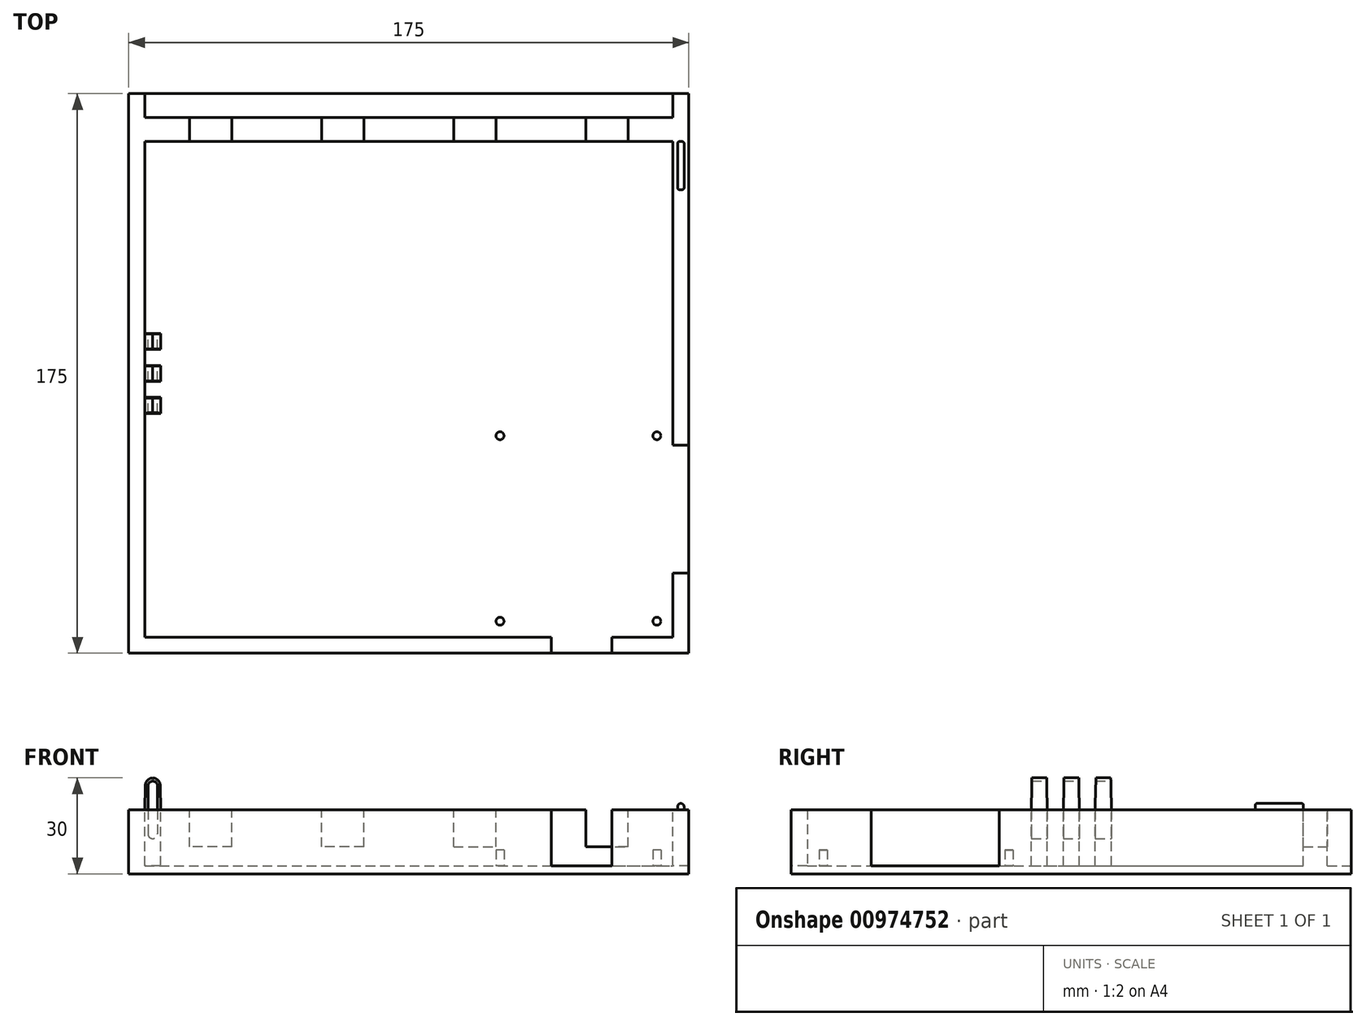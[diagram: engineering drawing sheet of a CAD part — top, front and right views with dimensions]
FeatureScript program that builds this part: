
annotation { "Feature Type Name" : "Feature", "Feature Type Description" : "" }
export const myFeature = defineFeature(function(context is Context, id is Id, definition is map)
    precondition{}
    {
        {
            var Q0;
            Q0=qCreatedBy(makeId("Top.planeOp"),FACE);
            var sketch = newSketch(context, id + "F0", { "sketchPlane" : qUnion([Q0])});
            skLineSegment(sketch, "E0.bottom", {"start": v(87.5, 87.5) * mm, "end": v(-87.5, 87.5) * mm});
            skLineSegment(sketch, "E0.top", {"start": v(87.5, -87.5) * mm, "end": v(-87.5, -87.5) * mm});
            skLineSegment(sketch, "E0.left", {"start": v(87.5, 87.5) * mm, "end": v(87.5, -87.5) * mm});
            skLineSegment(sketch, "E0.right", {"start": v(-87.5, 87.5) * mm, "end": v(-87.5, -87.5) * mm});
            skPoint(sketch, "E0.middle", {"position": v(0, 0) * mm});
            skSolve(sketch);
        }
        {
            var Q0;
            Q0 = qSketchRegion(id + "F0", true);
            extrude(context, id + "F1", {"entities" : qUnion([Q0]), "depth" : 20 * mm, "offsetDistance" : 25 * mm});
        }
        {
            var Q0;
            Q0=makeQuery(id+"F1.opExtrude","CAP_FACE",FACE,{"disambiguationData":[OSD([sQuery(id+"F0.wireOp",EDGE,"E0.bottom"),sQuery(id+"F0.wireOp",EDGE,"E0.top"),sQuery(id+"F0.wireOp",EDGE,"E0.left"),sQuery(id+"F0.wireOp",EDGE,"E0.right")])],"isStart":false});
            var sketch = newSketch(context, id + "F2", { "sketchPlane" : qUnion([Q0])});
            skLineSegment(sketch, "E1.bottom", {"start": v(-82.5, -82.5) * mm, "end": v(82.5, -82.5) * mm});
            skLineSegment(sketch, "E1.top", {"start": v(-82.5, 72.5) * mm, "end": v(82.5, 72.5) * mm});
            skLineSegment(sketch, "E1.left", {"start": v(-82.5, -82.5) * mm, "end": v(-82.5, 72.5) * mm});
            skLineSegment(sketch, "E1.right", {"start": v(82.5, -82.5) * mm, "end": v(82.5, 72.5) * mm});
            skSolve(sketch);
        }
        {
            var Q0;
            Q0 = qSketchRegion(id + "F2", true);
            extrude(context, id + "F3", {"entities" : qUnion([Q0]), "operationType" : NewBodyOperationType.REMOVE, "oppositeDirection" : true, "depth" : 17.5 * mm, "offsetDistance" : 25 * mm});
        }
        {
            var Q0;
            Q0=makeQuery(id+"F3.boolean.opBoolean","COPY",FACE,{"derivedFrom":makeQuery(id+"F3.opExtrude","CAP_FACE",FACE,{"disambiguationData":[OSD([sQuery(id+"F2.wireOp",EDGE,"E1.bottom"),sQuery(id+"F2.wireOp",EDGE,"E1.top"),sQuery(id+"F2.wireOp",EDGE,"E1.left"),sQuery(id+"F2.wireOp",EDGE,"E1.right")])],"isStart":false})});
            var sketch = newSketch(context, id + "F4", { "sketchPlane" : qUnion([Q0])});
            skCircle(sketch, "E2", {"center": v(28.5, -77.5) * mm, "radius": 1.25 * mm});
            skLineSegment(sketch, "E3", {"start": v(28.5, -77.5) * mm, "end": v(77.5, -77.5) * mm, "construction": true});
            skLineSegment(sketch, "E4", {"start": v(28.5, -77.5) * mm, "end": v(28.5, -6.05) * mm, "construction": true});
            skCircle(sketch, "E5", {"center": v(28.5, -19.5) * mm, "radius": 1.25 * mm});
            skCircle(sketch, "E6", {"center": v(77.5, -77.5) * mm, "radius": 1.25 * mm});
            skLineSegment(sketch, "E7", {"start": v(23.98, -19.5) * mm, "end": v(28.5, -19.5) * mm, "construction": true});
            skLineSegment(sketch, "E8", {"start": v(77.5, -77.5) * mm, "end": v(77.5, -2.25) * mm, "construction": true});
            skCircle(sketch, "E9", {"center": v(77.5, -19.5) * mm, "radius": 1.25 * mm});
            skSolve(sketch);
        }
        {
            var Q0;
            Q0 = qSketchRegion(id + "F4", true);
            extrude(context, id + "F5", {"entities" : qUnion([Q0]), "operationType" : NewBodyOperationType.ADD, "depth" : 5 * mm, "offsetDistance" : 25 * mm});
        }
        {
            var Q0;
            Q0=makeQuery(id+"F1.opExtrude","CAP_FACE",FACE,{"disambiguationData":[OSD([sQuery(id+"F0.wireOp",EDGE,"E0.bottom"),sQuery(id+"F0.wireOp",EDGE,"E0.top"),sQuery(id+"F0.wireOp",EDGE,"E0.left"),sQuery(id+"F0.wireOp",EDGE,"E0.right")])],"isStart":false});
            var sketch = newSketch(context, id + "F6", { "sketchPlane" : qUnion([Q0])});
            skLineSegment(sketch, "E10.bottom", {"start": v(-82.5, 80) * mm, "end": v(82.5, 80) * mm});
            skLineSegment(sketch, "E10.top", {"start": v(-82.5, 87.5) * mm, "end": v(82.5, 87.5) * mm});
            skLineSegment(sketch, "E10.left", {"start": v(-82.5, 80) * mm, "end": v(-82.5, 87.5) * mm});
            skLineSegment(sketch, "E10.right", {"start": v(82.5, 80) * mm, "end": v(82.5, 87.5) * mm});
            skSolve(sketch);
        }
        {
            var Q0;
            Q0 = qSketchRegion(id + "F6", true);
            extrude(context, id + "F7", {"entities" : qUnion([Q0]), "operationType" : NewBodyOperationType.REMOVE, "oppositeDirection" : true, "depth" : 17.5 * mm, "offsetDistance" : 25 * mm});
        }
        {
            var Q0;
            Q0=makeQuery(id+"F7.boolean.opBoolean","COPY",FACE,{"derivedFrom":makeQuery(id+"F7.opExtrude","SWEPT_FACE",FACE,{"disambiguationData":[OSD([sQuery(id+"F6.wireOp",EDGE,"E10.bottom")])]})});
            var sketch = newSketch(context, id + "F8", { "sketchPlane" : qUnion([Q0])});
            skLineSegment(sketch, "E11", {"start": v(-82.5, 11.25) * mm, "end": v(82.5, 11.25) * mm, "construction": true});
            skLineSegment(sketch, "E12", {"start": v(0, 20) * mm, "end": v(0, 2.5) * mm, "construction": true});
            skPoint(sketch, "E13", {"position": v(0, 11.25) * mm});
            skPoint(sketch, "E14", {"position": v(41.25, 11.25) * mm});
            skPoint(sketch, "E15", {"position": v(-41.25, 11.25) * mm});
            skPoint(sketch, "E16", {"position": v(-61.87, 11.25) * mm});
            skPoint(sketch, "E17", {"position": v(-20.62, 11.25) * mm});
            skPoint(sketch, "E18", {"position": v(20.62, 11.25) * mm});
            skPoint(sketch, "E19", {"position": v(61.87, 11.25) * mm});
            skLineSegment(sketch, "E20.bottom", {"start": v(-55.27, 14.1) * mm, "end": v(-68.47, 14.1) * mm});
            skLineSegment(sketch, "E20.top", {"start": v(-55.27, 8.4) * mm, "end": v(-68.47, 8.4) * mm});
            skLineSegment(sketch, "E20.left", {"start": v(-55.27, 14.1) * mm, "end": v(-55.27, 8.4) * mm});
            skLineSegment(sketch, "E20.right", {"start": v(-68.47, 14.1) * mm, "end": v(-68.47, 8.4) * mm});
            skLineSegment(sketch, "E21.bottom", {"start": v(-27.22, 14.1) * mm, "end": v(-14.02, 14.1) * mm});
            skLineSegment(sketch, "E21.top", {"start": v(-27.22, 8.4) * mm, "end": v(-14.02, 8.4) * mm});
            skLineSegment(sketch, "E21.left", {"start": v(-27.22, 14.1) * mm, "end": v(-27.22, 8.4) * mm});
            skLineSegment(sketch, "E21.right", {"start": v(-14.02, 14.1) * mm, "end": v(-14.02, 8.4) * mm});
            skLineSegment(sketch, "E22.bottom", {"start": v(27.22, 14.1) * mm, "end": v(14.02, 14.1) * mm});
            skLineSegment(sketch, "E22.top", {"start": v(27.22, 8.4) * mm, "end": v(14.02, 8.4) * mm});
            skLineSegment(sketch, "E22.left", {"start": v(27.22, 14.1) * mm, "end": v(27.22, 8.4) * mm});
            skLineSegment(sketch, "E22.right", {"start": v(14.02, 14.1) * mm, "end": v(14.02, 8.4) * mm});
            skLineSegment(sketch, "E23.bottom", {"start": v(68.47, 14.1) * mm, "end": v(55.27, 14.1) * mm});
            skLineSegment(sketch, "E23.top", {"start": v(68.47, 8.4) * mm, "end": v(55.27, 8.4) * mm});
            skLineSegment(sketch, "E23.left", {"start": v(68.47, 14.1) * mm, "end": v(68.47, 8.4) * mm});
            skLineSegment(sketch, "E23.right", {"start": v(55.27, 14.1) * mm, "end": v(55.27, 8.4) * mm});
            skSolve(sketch);
        }
        {
            var Q0;
            Q0 = qSketchRegion(id + "F8", true);
            extrude(context, id + "F9", {"entities" : qUnion([Q0]), "operationType" : NewBodyOperationType.REMOVE, "oppositeDirection" : true, "depth" : 8.5 * mm, "offsetDistance" : 25 * mm});
        }
        {
            var Q0;
            Q0=makeQuery(id+"F1.opExtrude","CAP_FACE",FACE,{"disambiguationData":[OSD([sQuery(id+"F0.wireOp",EDGE,"E0.bottom"),sQuery(id+"F0.wireOp",EDGE,"E0.top"),sQuery(id+"F0.wireOp",EDGE,"E0.left"),sQuery(id+"F0.wireOp",EDGE,"E0.right")])],"isStart":false});
            var sketch = newSketch(context, id + "F10", { "sketchPlane" : qUnion([Q0])});
            skLineSegment(sketch, "E24.bottom", {"start": v(-77.5, -2.5) * mm, "end": v(-82.5, -2.5) * mm});
            skLineSegment(sketch, "E24.top", {"start": v(-77.5, 2.5) * mm, "end": v(-82.5, 2.5) * mm});
            skLineSegment(sketch, "E24.left", {"start": v(-77.5, -2.5) * mm, "end": v(-77.5, 2.5) * mm});
            skLineSegment(sketch, "E24.right", {"start": v(-82.5, -2.5) * mm, "end": v(-82.5, 2.5) * mm});
            skLineSegment(sketch, "E25.bottom", {"start": v(-77.5, 7.5) * mm, "end": v(-82.5, 7.5) * mm});
            skLineSegment(sketch, "E25.top", {"start": v(-77.5, 12.5) * mm, "end": v(-82.5, 12.5) * mm});
            skLineSegment(sketch, "E25.left", {"start": v(-77.5, 7.5) * mm, "end": v(-77.5, 12.5) * mm});
            skLineSegment(sketch, "E25.right", {"start": v(-82.5, 7.5) * mm, "end": v(-82.5, 12.5) * mm});
            skLineSegment(sketch, "E26.bottom", {"start": v(-77.5, -12.5) * mm, "end": v(-82.5, -12.5) * mm});
            skLineSegment(sketch, "E26.top", {"start": v(-77.5, -7.5) * mm, "end": v(-82.5, -7.5) * mm});
            skLineSegment(sketch, "E26.left", {"start": v(-77.5, -12.5) * mm, "end": v(-77.5, -7.5) * mm});
            skLineSegment(sketch, "E26.right", {"start": v(-82.5, -12.5) * mm, "end": v(-82.5, -7.5) * mm});
            skSolve(sketch);
        }
        {
            var Q0;
            Q0 = qSketchRegion(id + "F10", true);
            extrude(context, id + "F11", {"entities" : qUnion([Q0]), "operationType" : NewBodyOperationType.ADD, "oppositeDirection" : true, "depth" : 17.5 * mm, "offsetDistance" : 25 * mm, "hasSecondDirection" : true, "secondDirectionOppositeDirection" : false, "secondDirectionDepth" : 10 * mm, "hasSecondDirectionDraft" : true, "secondDirectionDraftAngle" : 1 * degree, "secondDirectionDraftPullDirection" : true});
        }
        {
            var Q0;
            Q0=makeQuery(id+"F11.opExtrude","CAP_EDGE",EDGE,{"disambiguationData":[OSD([sQuery(id+"F10.wireOp",EDGE,"E25.right")])],"isStart":true});
            var Q1;
            Q1=makeQuery(id+"F11.opExtrude","CAP_EDGE",EDGE,{"disambiguationData":[OSD([sQuery(id+"F10.wireOp",EDGE,"E25.left")])],"isStart":true});
            var Q2;
            Q2=makeQuery(id+"F11.opExtrude","CAP_EDGE",EDGE,{"disambiguationData":[OSD([sQuery(id+"F10.wireOp",EDGE,"E24.left")])],"isStart":true});
            var Q3;
            Q3=makeQuery(id+"F11.opExtrude","CAP_EDGE",EDGE,{"disambiguationData":[OSD([sQuery(id+"F10.wireOp",EDGE,"E24.right")])],"isStart":true});
            var Q4;
            Q4=makeQuery(id+"F11.opExtrude","CAP_EDGE",EDGE,{"disambiguationData":[OSD([sQuery(id+"F10.wireOp",EDGE,"E26.right")])],"isStart":true});
            var Q5;
            Q5=makeQuery(id+"F11.opExtrude","CAP_EDGE",EDGE,{"disambiguationData":[OSD([sQuery(id+"F10.wireOp",EDGE,"E26.left")])],"isStart":true});
            fillet(context, id + "F12", {"entities" : qUnion([Q0, Q1, Q2, Q3, Q4, Q5]), "radius" : 2.5 * mm, "tangentPropagation" : true, "allowEdgeOverflow" : false});
        }
        {
            var Q0;
            Q0=makeQuery(id+"F11.*.split.splitOp","SPLIT",FACE,{"derivedFrom":makeQuery(id+"F11.opExtrude","SWEPT_FACE",FACE,{"disambiguationData":[OSD([sQuery(id+"F10.wireOp",EDGE,"E25.top")])]})});
            var sketch = newSketch(context, id + "F13", { "sketchPlane" : qUnion([Q0])});
            skLineSegment(sketch, "E27.left", {"start": v(81.5, 27.5) * mm, "end": v(81.5, 12.5) * mm});
            skLineSegment(sketch, "E27.right", {"start": v(78.5, 27.5) * mm, "end": v(78.5, 12.5) * mm});
            skPoint(sketch, "E27.middle", {"position": v(80, 20) * mm});
            skArc(sketch, "E28", {"start": v(81.5, 27.5) * mm, "mid": v(80, 29) * mm, "end": v(78.5, 27.5) * mm});
            skArc(sketch, "E29", {"start": v(78.5, 12.5) * mm, "mid": v(80, 11) * mm, "end": v(81.5, 12.5) * mm});
            skSolve(sketch);
        }
        {
            var Q0;
            Q0 = qSketchRegion(id + "F13", true);
            extrude(context, id + "F14", {"entities" : qUnion([Q0]), "operationType" : NewBodyOperationType.REMOVE, "oppositeDirection" : true, "depth" : 25 * mm, "offsetDistance" : 25 * mm});
        }
        {
            var Q0;
            Q0=makeQuery(id+"F1.opExtrude","CAP_FACE",FACE,{"disambiguationData":[OSD([sQuery(id+"F0.wireOp",EDGE,"E0.bottom"),sQuery(id+"F0.wireOp",EDGE,"E0.top"),sQuery(id+"F0.wireOp",EDGE,"E0.left"),sQuery(id+"F0.wireOp",EDGE,"E0.right")])],"isStart":false});
            var sketch = newSketch(context, id + "F15", { "sketchPlane" : qUnion([Q0])});
            skLineSegment(sketch, "E30.bottom", {"start": v(63.5, -73.66) * mm, "end": v(44.5, -73.66) * mm});
            skLineSegment(sketch, "E30.top", {"start": v(63.5, -91.34) * mm, "end": v(44.5, -91.34) * mm});
            skLineSegment(sketch, "E30.left", {"start": v(63.5, -73.66) * mm, "end": v(63.5, -91.34) * mm});
            skLineSegment(sketch, "E30.right", {"start": v(44.5, -73.66) * mm, "end": v(44.5, -91.34) * mm});
            skPoint(sketch, "E30.middle", {"position": v(54, -82.5) * mm});
            skLineSegment(sketch, "E31.bottom", {"start": v(98.64, -22.5) * mm, "end": v(66.36, -22.5) * mm});
            skLineSegment(sketch, "E31.top", {"start": v(98.64, -62.5) * mm, "end": v(66.36, -62.5) * mm});
            skLineSegment(sketch, "E31.left", {"start": v(98.64, -22.5) * mm, "end": v(98.64, -62.5) * mm});
            skLineSegment(sketch, "E31.right", {"start": v(66.36, -22.5) * mm, "end": v(66.36, -62.5) * mm});
            skPoint(sketch, "E31.middle", {"position": v(82.5, -42.5) * mm});
            skSolve(sketch);
        }
        {
            var Q0;
            Q0 = qSketchRegion(id + "F15", true);
            extrude(context, id + "F16", {"entities" : qUnion([Q0]), "operationType" : NewBodyOperationType.REMOVE, "oppositeDirection" : true, "depth" : 17.5 * mm, "offsetDistance" : 25 * mm});
        }
        {
            var Q0;
            Q0=makeQuery(id+"F7.boolean.opBoolean","COPY",FACE,{"derivedFrom":makeQuery(id+"F7.opExtrude","SWEPT_FACE",FACE,{"disambiguationData":[OSD([sQuery(id+"F6.wireOp",EDGE,"E10.bottom")])]})});
            var sketch = newSketch(context, id + "F17", { "sketchPlane" : qUnion([Q0])});
            skLineSegment(sketch, "E32", {"start": v(-68.47, 14.1) * mm, "end": v(-68.47, 20) * mm});
            skLineSegment(sketch, "E33", {"start": v(-68.47, 20) * mm, "end": v(-55.28, 20) * mm});
            skLineSegment(sketch, "E34", {"start": v(-55.28, 20) * mm, "end": v(-55.28, 14.1) * mm});
            skLineSegment(sketch, "E35.bottom", {"start": v(-27.22, 14.1) * mm, "end": v(-14.02, 14.1) * mm});
            skLineSegment(sketch, "E35.top", {"start": v(-27.22, 20) * mm, "end": v(-14.02, 20) * mm});
            skLineSegment(sketch, "E35.left", {"start": v(-27.22, 14.1) * mm, "end": v(-27.22, 20) * mm});
            skLineSegment(sketch, "E35.right", {"start": v(-14.02, 14.1) * mm, "end": v(-14.02, 20) * mm});
            skLineSegment(sketch, "E36.bottom", {"start": v(14.02, 14.1) * mm, "end": v(27.22, 14.1) * mm});
            skLineSegment(sketch, "E36.top", {"start": v(14.02, 20) * mm, "end": v(27.22, 20) * mm});
            skLineSegment(sketch, "E36.left", {"start": v(14.02, 14.1) * mm, "end": v(14.02, 20) * mm});
            skLineSegment(sketch, "E36.right", {"start": v(27.22, 14.1) * mm, "end": v(27.22, 20) * mm});
            skLineSegment(sketch, "E37.bottom", {"start": v(55.27, 14.1) * mm, "end": v(68.47, 14.1) * mm});
            skLineSegment(sketch, "E37.top", {"start": v(55.27, 20) * mm, "end": v(68.47, 20) * mm});
            skLineSegment(sketch, "E37.left", {"start": v(55.27, 14.1) * mm, "end": v(55.27, 20) * mm});
            skLineSegment(sketch, "E37.right", {"start": v(68.47, 14.1) * mm, "end": v(68.47, 20) * mm});
            skLineSegment(sketch, "E38", {"start": v(-68.47, 14.1) * mm, "end": v(-55.27, 14.1) * mm});
            skSolve(sketch);
        }
        {
            var Q0;
            Q0 = qSketchRegion(id + "F17", true);
            extrude(context, id + "F18", {"entities" : qUnion([Q0]), "operationType" : NewBodyOperationType.REMOVE, "oppositeDirection" : true, "depth" : 8.5 * mm, "offsetDistance" : 25 * mm});
        }
        {
            var Q0;
            {var subQ2=sQuery(id+"F0.wireOp",EDGE,"E0.right");var subQ3=makeQuery(id+"F1.opExtrude","SWEPT_FACE",FACE,{"disambiguationData":[OSD([subQ2])]});var subQ5=sQuery(id+"F0.wireOp",EDGE,"E0.bottom");var subQ6=makeQuery(id+"F1.opExtrude","SWEPT_FACE",FACE,{"disambiguationData":[OSD([subQ5])]});var subQ9=sQuery(id+"F0.wireOp",EDGE,"E0.top");var subQ10=sQuery(id+"F0.wireOp",EDGE,"E0.left");Q0=makeQuery(id+"F18.boolean.opBoolean","SPLIT",FACE,{"disambiguationData":[TD([subQ3])],"derivedFrom":makeQuery(id+"F16.boolean.opBoolean","SPLIT",FACE,{"disambiguationData":[TD([subQ6])],"derivedFrom":makeQuery(id+"F1.opExtrude","CAP_FACE",FACE,{"disambiguationData":[OSD([subQ5,subQ9,subQ10,subQ2])],"isStart":false})})});}
            var sketch = newSketch(context, id + "F19", { "sketchPlane" : qUnion([Q0])});
            skLineSegment(sketch, "E39.bottom", {"start": v(86, 72.5) * mm, "end": v(84, 72.5) * mm});
            skLineSegment(sketch, "E39.top", {"start": v(86, 57.5) * mm, "end": v(84, 57.5) * mm});
            skLineSegment(sketch, "E39.left", {"start": v(86, 72.5) * mm, "end": v(86, 57.5) * mm});
            skLineSegment(sketch, "E39.right", {"start": v(84, 72.5) * mm, "end": v(84, 57.5) * mm});
            skLineSegment(sketch, "E40", {"start": v(85, 72.5) * mm, "end": v(85, 57.5) * mm, "construction": true});
            skLineSegment(sketch, "E41", {"start": v(84, 65) * mm, "end": v(86, 65) * mm, "construction": true});
            skPoint(sketch, "E42", {"position": v(85, 65) * mm});
            skPoint(sketch, "E43", {"position": v(87.5, 65) * mm});
            skPoint(sketch, "E44", {"position": v(82.5, 65) * mm});
            skSolve(sketch);
        }
        {
            var Q0;
            Q0 = qSketchRegion(id + "F19", true);
            extrude(context, id + "F20", {"entities" : qUnion([Q0]), "operationType" : NewBodyOperationType.ADD, "depth" : 2 * mm, "offsetDistance" : 25 * mm});
        }
        {
            var Q0;
            Q0=makeQuery(id+"F20.opExtrude","CAP_EDGE",EDGE,{"disambiguationData":[OSD([sQuery(id+"F19.wireOp",EDGE,"E39.right")])],"isStart":false});
            var Q1;
            Q1=makeQuery(id+"F20.opExtrude","CAP_EDGE",EDGE,{"disambiguationData":[OSD([sQuery(id+"F19.wireOp",EDGE,"E39.left")])],"isStart":false});
            fillet(context, id + "F21", {"entities" : qUnion([Q0, Q1]), "radius" : 1 * mm, "tangentPropagation" : true, "allowEdgeOverflow" : false});
        }
        {
            var Q0;
            Q0=makeQuery(id+"F21.opFillet","BLEND_EDGE",EDGE,{"blendedFrom":[makeQuery(id+"F20.opExtrude","CAP_EDGE",EDGE,{"disambiguationData":[OSD([sQuery(id+"F19.wireOp",EDGE,"E39.left")])],"isStart":false}),makeQuery(id+"F20.opExtrude","SWEPT_FACE",FACE,{"disambiguationData":[OSD([sQuery(id+"F19.wireOp",EDGE,"E39.top")])]})],"blendedInto":[makeQuery(id+"F20.opExtrude","SWEPT_FACE",FACE,{"disambiguationData":[OSD([sQuery(id+"F19.wireOp",EDGE,"E39.top")])]})]});
            var Q1;
            Q1=makeQuery(id+"F21.opFillet","BLEND_EDGE",EDGE,{"blendedFrom":[makeQuery(id+"F20.opExtrude","CAP_EDGE",EDGE,{"disambiguationData":[OSD([sQuery(id+"F19.wireOp",EDGE,"E39.left")])],"isStart":false}),makeQuery(id+"F20.opExtrude","SWEPT_FACE",FACE,{"disambiguationData":[OSD([sQuery(id+"F19.wireOp",EDGE,"E39.bottom")])]})],"blendedInto":[makeQuery(id+"F20.opExtrude","SWEPT_FACE",FACE,{"disambiguationData":[OSD([sQuery(id+"F19.wireOp",EDGE,"E39.bottom")])]})]});
            fillet(context, id + "F22", {"entities" : qUnion([Q0, Q1]), "radius" : 0.5 * mm, "tangentPropagation" : true, "allowEdgeOverflow" : false});
        }
    });
